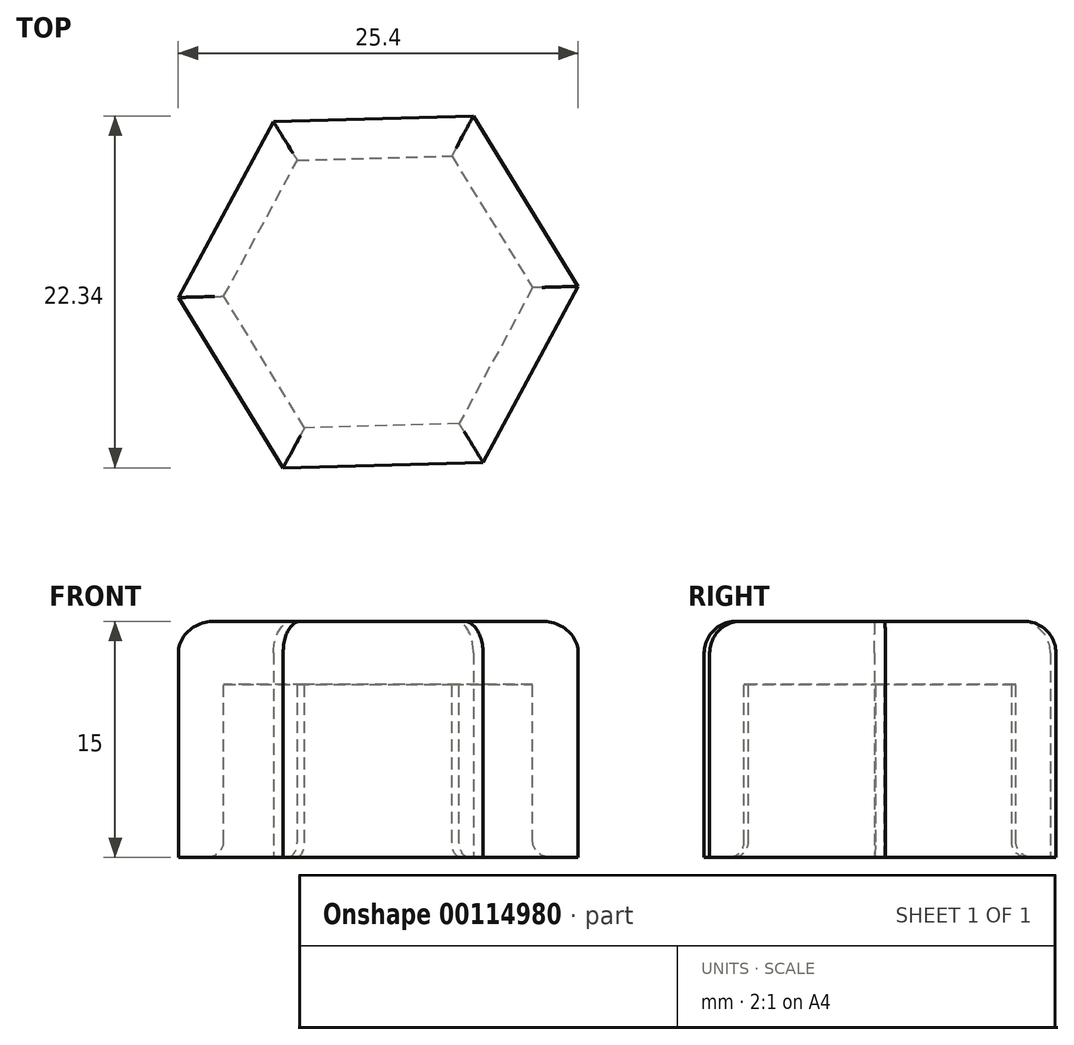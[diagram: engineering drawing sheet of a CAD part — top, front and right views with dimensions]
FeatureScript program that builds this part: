
annotation { "Feature Type Name" : "Feature", "Feature Type Description" : "" }
export const myFeature = defineFeature(function(context is Context, id is Id, definition is map)
    precondition{}
    {
        {
            var Q0;
            Q0=qCreatedBy(makeId("Top.planeOp"),FACE);
            var sketch = newSketch(context, id + "F0", { "sketchPlane" : qUnion([Q0])});
            skCircle(sketch, "E0.cCircle", {"center": v(0, 0) * mm, "radius": 8.5 * mm, "construction": true});
            skLineSegment(sketch, "E0.0", {"start": v(-9.81, -0.27) * mm, "end": v(-5.14, 8.36) * mm});
            skLineSegment(sketch, "E0.1", {"start": v(-5.14, 8.36) * mm, "end": v(4.67, 8.63) * mm});
            skLineSegment(sketch, "E0.2", {"start": v(4.67, 8.63) * mm, "end": v(9.81, 0.27) * mm});
            skLineSegment(sketch, "E0.3", {"start": v(9.81, 0.27) * mm, "end": v(5.14, -8.36) * mm});
            skLineSegment(sketch, "E0.4", {"start": v(5.14, -8.36) * mm, "end": v(-4.67, -8.63) * mm});
            skLineSegment(sketch, "E0.5", {"start": v(-4.67, -8.63) * mm, "end": v(-9.81, -0.27) * mm});
            skPoint(sketch, "E0.0.midPoint", {"position": v(-7.48, 4.04) * mm});
            skLineSegment(sketch, "E1.0", {"start": v(-6.04, -11.17) * mm, "end": v(-12.7, -0.35) * mm});
            skLineSegment(sketch, "E1.1", {"start": v(-6.65, 10.82) * mm, "end": v(6.04, 11.17) * mm});
            skLineSegment(sketch, "E1.2", {"start": v(6.04, 11.17) * mm, "end": v(12.7, 0.35) * mm});
            skLineSegment(sketch, "E1.3", {"start": v(-12.7, -0.35) * mm, "end": v(-6.65, 10.82) * mm});
            skLineSegment(sketch, "E1.4", {"start": v(12.7, 0.35) * mm, "end": v(6.65, -10.82) * mm});
            skLineSegment(sketch, "E1.5", {"start": v(6.65, -10.82) * mm, "end": v(-6.04, -11.17) * mm});
            skSolve(sketch);
        }
        {
            var Q0;
            Q0 = qSketchRegion(id + "F0", true);
            var Q1;
            Q1=makeQuery(id+"F0.imprint","IMPRINT",FACE,{"disambiguationData":[TD([[makeQuery(id+"F0.imprint","IMPRINT",EDGE,{"derivedFrom":sQuery(id+"F0.wireOp",EDGE,"E0.0")}),-1.0]])]});
            extrude(context, id + "F1", {"entities" : qUnion([Q0, Q1]), "depth" : 4 * mm});
        }
        {
            var Q0;
            Q0=makeQuery(id+"F0.imprint","IMPRINT",FACE,{"disambiguationData":[TD([[makeQuery(id+"F0.imprint","IMPRINT",EDGE,{"derivedFrom":sQuery(id+"F0.wireOp",EDGE,"E0.0")}),1.0]])]});
            extrude(context, id + "F2", {"entities" : qUnion([Q0]), "operationType" : NewBodyOperationType.ADD, "oppositeDirection" : true, "depth" : 11 * mm});
        }
        {
            var Q0;
            Q0=makeQuery(id+"F1.opExtrude","CAP_FACE",FACE,{"disambiguationData":[OSD([sQuery(id+"F0.wireOp",EDGE,"E1.0"),sQuery(id+"F0.wireOp",EDGE,"E1.1"),sQuery(id+"F0.wireOp",EDGE,"E1.2"),sQuery(id+"F0.wireOp",EDGE,"E1.3"),sQuery(id+"F0.wireOp",EDGE,"E1.4"),sQuery(id+"F0.wireOp",EDGE,"E1.5")])],"isStart":false});
            var Q1;
            Q1=makeQuery(id+"F1.opExtrude","CAP_EDGE",EDGE,{"disambiguationData":[OSD([sQuery(id+"F0.wireOp",EDGE,"E1.4")])],"isStart":false});
            fillet(context, id + "F3", {"entities" : qUnion([Q0, Q1]), "radius" : 2 * mm, "tangentPropagation" : true, "allowEdgeOverflow" : false});
        }
        {
            var Q0;
            Q0=makeQuery(id+"F2.opExtrude","CAP_EDGE",EDGE,{"disambiguationData":[OSD([sQuery(id+"F0.wireOp",EDGE,"E0.1")])],"isStart":false});
            var Q1;
            Q1=makeQuery(id+"F2.opExtrude","CAP_EDGE",EDGE,{"disambiguationData":[OSD([sQuery(id+"F0.wireOp",EDGE,"E0.0")])],"isStart":false});
            var Q2;
            Q2=makeQuery(id+"F2.opExtrude","CAP_EDGE",EDGE,{"disambiguationData":[OSD([sQuery(id+"F0.wireOp",EDGE,"E0.5")])],"isStart":false});
            var Q3;
            Q3=makeQuery(id+"F2.opExtrude","CAP_EDGE",EDGE,{"disambiguationData":[OSD([sQuery(id+"F0.wireOp",EDGE,"E0.4")])],"isStart":false});
            var Q4;
            Q4=makeQuery(id+"F2.opExtrude","CAP_EDGE",EDGE,{"disambiguationData":[OSD([sQuery(id+"F0.wireOp",EDGE,"E0.3")])],"isStart":false});
            var Q5;
            Q5=makeQuery(id+"F2.opExtrude","CAP_EDGE",EDGE,{"disambiguationData":[OSD([sQuery(id+"F0.wireOp",EDGE,"E0.2")])],"isStart":false});
            fillet(context, id + "F4", {"entities" : qUnion([Q0, Q1, Q2, Q3, Q4, Q5]), "radius" : 1 * mm, "tangentPropagation" : true, "allowEdgeOverflow" : false});
        }
    });
